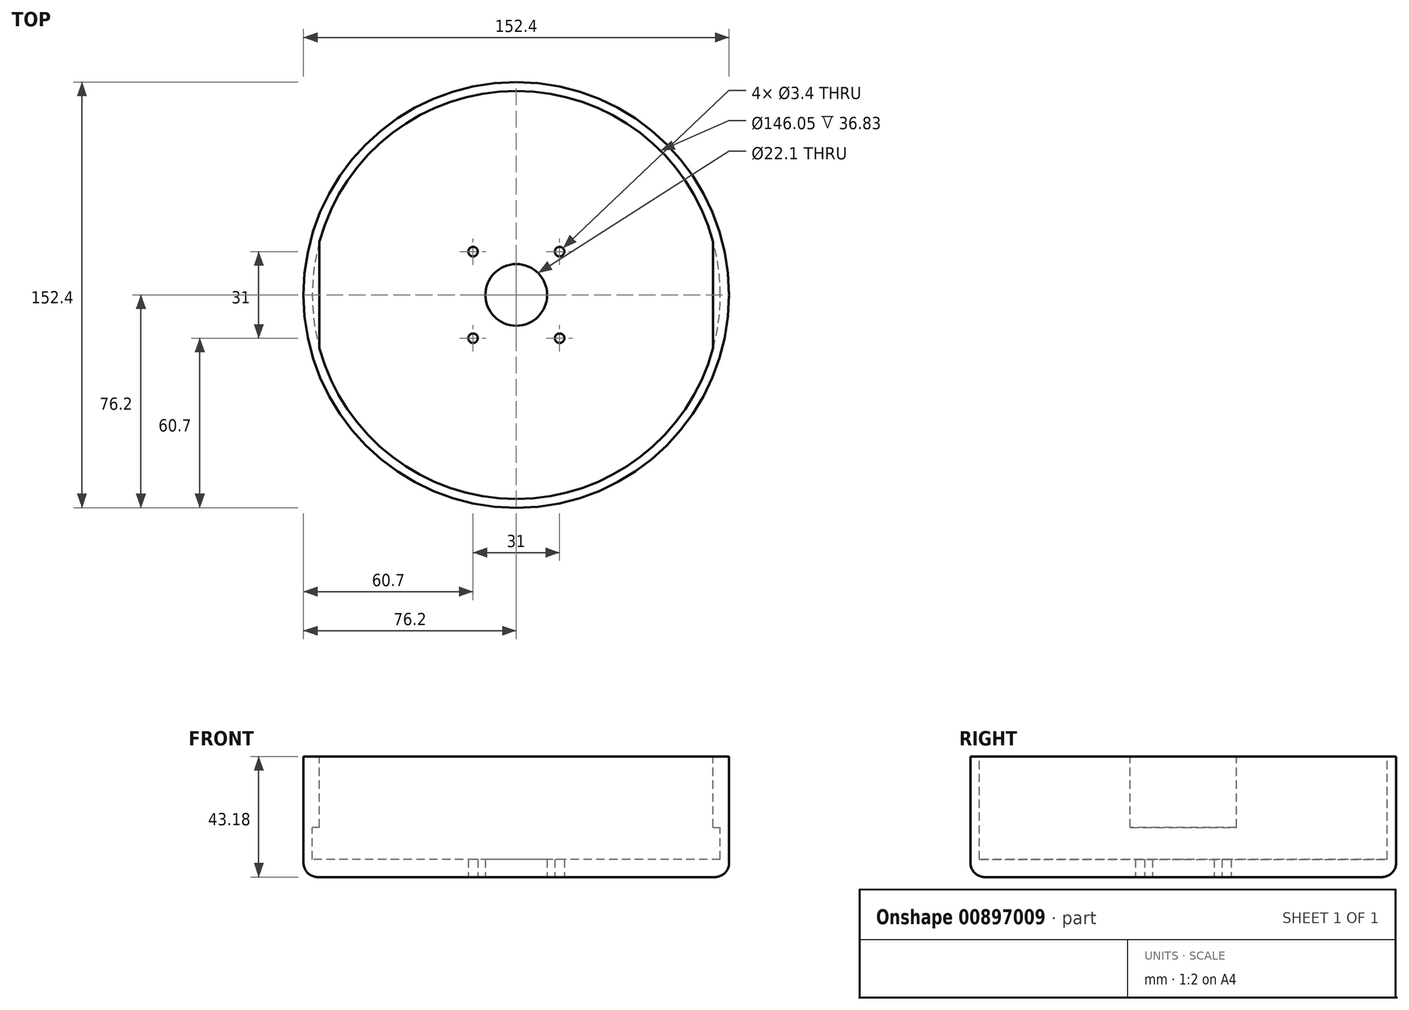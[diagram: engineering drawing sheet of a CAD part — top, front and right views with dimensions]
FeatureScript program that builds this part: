
annotation { "Feature Type Name" : "Feature", "Feature Type Description" : "" }
export const myFeature = defineFeature(function(context is Context, id is Id, definition is map)
    precondition{}
    {
        {
            var Q0;
            Q0=qCreatedBy(makeId("Top.planeOp"),FACE);
            var sketch = newSketch(context, id + "F0", { "sketchPlane" : qUnion([Q0])});
            skCircle(sketch, "E0", {"center": v(0, 0) * mm, "radius": 76.2 * mm});
            skSolve(sketch);
        }
        {
            var Q0;
            Q0 = qSketchRegion(id + "F0", true);
            extrude(context, id + "F1", {"entities" : qUnion([Q0]), "depth" : 43.18 * mm, "offsetDistance" : 25.4 * mm});
        }
        {
            var Q0;
            Q0=makeQuery(id+"F1.opExtrude","CAP_FACE",FACE,{"disambiguationData":[OSD([sQuery(id+"F0.wireOp",EDGE,"E0")])],"isStart":false});
            var sketch = newSketch(context, id + "F2", { "sketchPlane" : qUnion([Q0])});
            skCircle(sketch, "E1", {"center": v(0, 0) * mm, "radius": 73.03 * mm});
            skSolve(sketch);
        }
        {
            var Q0;
            Q0 = qSketchRegion(id + "F2", true);
            extrude(context, id + "F3", {"entities" : qUnion([Q0]), "operationType" : NewBodyOperationType.REMOVE, "oppositeDirection" : true, "depth" : 36.83 * mm, "offsetDistance" : 25.4 * mm});
        }
        {
            var Q0;
            Q0=makeQuery(id+"F1.opExtrude","CAP_FACE",FACE,{"disambiguationData":[OSD([sQuery(id+"F0.wireOp",EDGE,"E0")])],"isStart":true});
            var sketch = newSketch(context, id + "F4", { "sketchPlane" : qUnion([Q0])});
            skCircle(sketch, "E2", {"center": v(0, 0) * mm, "radius": 11.05 * mm});
            skSolve(sketch);
        }
        {
            var Q0;
            Q0 = qSketchRegion(id + "F4", true);
            extrude(context, id + "F5", {"entities" : qUnion([Q0]), "operationType" : NewBodyOperationType.REMOVE, "oppositeDirection" : true, "depth" : 25.4 * mm, "offsetDistance" : 25.4 * mm});
        }
        {
            var Q0;
            Q0=makeQuery(id+"F1.opExtrude","CAP_FACE",FACE,{"disambiguationData":[OSD([sQuery(id+"F0.wireOp",EDGE,"E0")])],"isStart":true});
            var sketch = newSketch(context, id + "F6", { "sketchPlane" : qUnion([Q0])});
            skLineSegment(sketch, "E3.bottom", {"start": v(15.5, -15.5) * mm, "end": v(-15.5, -15.5) * mm, "construction": true});
            skLineSegment(sketch, "E3.top", {"start": v(15.5, 15.5) * mm, "end": v(-15.5, 15.5) * mm, "construction": true});
            skLineSegment(sketch, "E3.left", {"start": v(15.5, -15.5) * mm, "end": v(15.5, 15.5) * mm, "construction": true});
            skLineSegment(sketch, "E3.right", {"start": v(-15.5, -15.5) * mm, "end": v(-15.5, 15.5) * mm, "construction": true});
            skPoint(sketch, "E3.middle", {"position": v(0, 0) * mm});
            skCircle(sketch, "E4", {"center": v(15.5, 15.5) * mm, "radius": 1.7 * mm});
            skCircle(sketch, "E5", {"center": v(15.5, -15.5) * mm, "radius": 1.7 * mm});
            skCircle(sketch, "E6", {"center": v(-15.5, -15.5) * mm, "radius": 1.7 * mm});
            skCircle(sketch, "E7", {"center": v(-15.5, 15.5) * mm, "radius": 1.7 * mm});
            skSolve(sketch);
        }
        {
            var Q0;
            Q0 = qSketchRegion(id + "F6", true);
            extrude(context, id + "F7", {"entities" : qUnion([Q0]), "operationType" : NewBodyOperationType.REMOVE, "endBound" : BoundingType.THROUGH_ALL, "oppositeDirection" : true, "depth" : 25.4 * mm, "offsetDistance" : 25.4 * mm});
        }
        {
            var Q0;
            Q0=makeQuery(id+"F1.opExtrude","CAP_EDGE",EDGE,{"disambiguationData":[OSD([sQuery(id+"F0.wireOp",EDGE,"E0")])],"isStart":true});
            fillet(context, id + "F8", {"entities" : qUnion([Q0]), "radius" : 5.08 * mm, "tangentPropagation" : true, "allowEdgeOverflow" : false});
        }
        {
            var Q0;
            Q0=makeQuery(id+"F1.opExtrude","CAP_FACE",FACE,{"disambiguationData":[OSD([sQuery(id+"F0.wireOp",EDGE,"E0")])],"isStart":false});
            var sketch = newSketch(context, id + "F9", { "sketchPlane" : qUnion([Q0])});
            skLineSegment(sketch, "E8", {"start": v(73.03, 0) * mm, "end": v(-73.03, 0) * mm, "construction": true});
            skLineSegment(sketch, "E9", {"start": v(-70.5, 19.05) * mm, "end": v(-70.5, 0) * mm});
            skLineSegment(sketch, "E10", {"start": v(-70.5, 0) * mm, "end": v(-70.5, -19.05) * mm});
            skLineSegment(sketch, "E11", {"start": v(0, 29.02) * mm, "end": v(0, -27.82) * mm, "construction": true});
            skLineSegment(sketch, "E12.MirrorCS", {"start": v(70.5, 19.05) * mm, "end": v(70.5, 0) * mm});
            skLineSegment(sketch, "E13.MirrorCS", {"start": v(70.5, 0) * mm, "end": v(70.5, -19.05) * mm});
            skSolve(sketch);
        }
        {
            var Q0;
            {var subQ0=sQuery(id+"F9.wireOp",EDGE,"E9");Q0=makeQuery(id+"F9.imprint","IMPRINT",FACE,{"disambiguationData":[TD([[makeQuery(id+"F9.imprint","IMPRINT",EDGE,{"derivedFrom":subQ0}),-1.0]])]});}
            var Q1;
            {var subQ0=sQuery(id+"F9.wireOp",EDGE,"E12.MirrorCS");Q1=makeQuery(id+"F9.imprint","IMPRINT",FACE,{"disambiguationData":[TD([[makeQuery(id+"F9.imprint","IMPRINT",EDGE,{"derivedFrom":subQ0}),1.0]])]});}
            extrude(context, id + "F10", {"entities" : qUnion([Q0, Q1]), "operationType" : NewBodyOperationType.ADD, "oppositeDirection" : true, "depth" : 25.4 * mm, "offsetDistance" : 25.4 * mm});
        }
    });
